# Revit family: Gira_545200
name_source: partatom
category: Elektroinstallationen
revit_build: Autodesk Revit 2017 (Build: 20160225_1515(x64)
units: mm (PartAtom-declared; Revit-internal decimal feet)

## family parameters
Basisbauteil = Fläche
Beim Laden mit Abzugskörper schneiden = Nein
Bemaßung runder Anschluss = Durchmesser verwenden
Beschriftungsausrichtung beibehalten = Nein
Gemeinsam genutzt = Nein
Raumberechnungspunkt = Nein
Teiletyp = Normal

## types (1)
- Funk Empfangsmodul REG Gira eNet
    Anzahl der Ausgänge = 0
    Anzahl der Eingänge = 0
    Anzahl der binären Eingänge = 0
    App-Steuerung über Bluetooth = Nein
    Art des Zubehörs = sonstige
    BIM = https://media.stage.bim.site X1 REG KNX.rfa
    BIMSITE_PRODUCT_ID = 9eb5853e0265f447f9b99469d575ccbd5280435d
    Beschreibung = eNet Funk Empfangsmodul  REG Merkmale:  Das eNet Funk Empfangsmodul ist ein Funkempfänger für max. 32 eNet Funk Reiheneinbaumodule.  Betrieb mit Spannungsversorgung.  Integrierte Antenne.  Externe Antenne zusätzlich anschließbar bei ungünstigen Einbaubedingungen.  Hinweise :  Die Funkzulassung gilt für Staaten der EU und EFTA.  Beim Einbau in Verteilerschrank bzw. Unterverteilung mit Metallgehäuse ist eine Zusatzantenne erforderlich. Die Zusatzantenne ist außerhalb des Metallgehäuses zu platzieren.
    Breite in Teilungseinheiten = 0
    Bussystem Funkbus = Nein
    Bussystem KNX = Nein
    Bussystem KNX-Funk = Nein
    Bussystem LON = Nein
    Bussystem Powernet = Nein
    Datenblatt = https://media.stage.bim.site
    Datenblatt 1 = https://media.stage.bim.site
    Dimmung Phasenabschnitt = Nein
    Dimmung Phasenanschnitt = Nein
    Funk bidirektional = Nein
    Funktion Schalten = Nein
    GTIN = 4010337774303
    Geeignet für C-Last = Nein
    HAN = 545200
    Halogenfrei = Nein
    HeinzeBIM = https://www.heinze.de
    Hersteller = Gira
    Kosten = 0 $
    Leistungszusatz verwendbar = Nein
    Lichtwertspeicher = Nein
    Max. Anzahl der Jalousieausgänge = 0
    Max. Anzahl der Schaltausgänge = 0
    Max. Schaltleistung [Voltampere] = 0
    Mit Beschriftungsfeld = Nein
    Mit Busankopplung = Nein
    Mit LED-Anzeige = Nein
    Modulare Erweiterungsmöglichkeit = Nein
    Nebenstelleneingang = Nein
    Parallel-Betrieb möglich = Nein
    Produktseite = https://media.stage.bim.site
    Seriendimmer = Nein
    Transparent = Nein
    Typname = Funk Empfangsmodul REG Gira eNet
    URL = https://www.gira.de
    Verschiedene Phasen anschließbar = Nein
    Verwendbar mit Bewegungsmelder = Nein
    Verwendbar mit Funktaste = Nein
    Verwendbar mit IR-Taste = Nein
    Verwendbar mit Präsenzmelder = Nein
    Verwendbar mit Taste = Nein
    Verwendbar mit Zeitschalter/Timer = Nein
    Vor Ort-/Handbedienung = Nein
    Vorgabe-Ansicht = 1219 mm

## geometry (parser evidence)
native form markers: Sweep x2
no freeform markers — native parametric forms only
